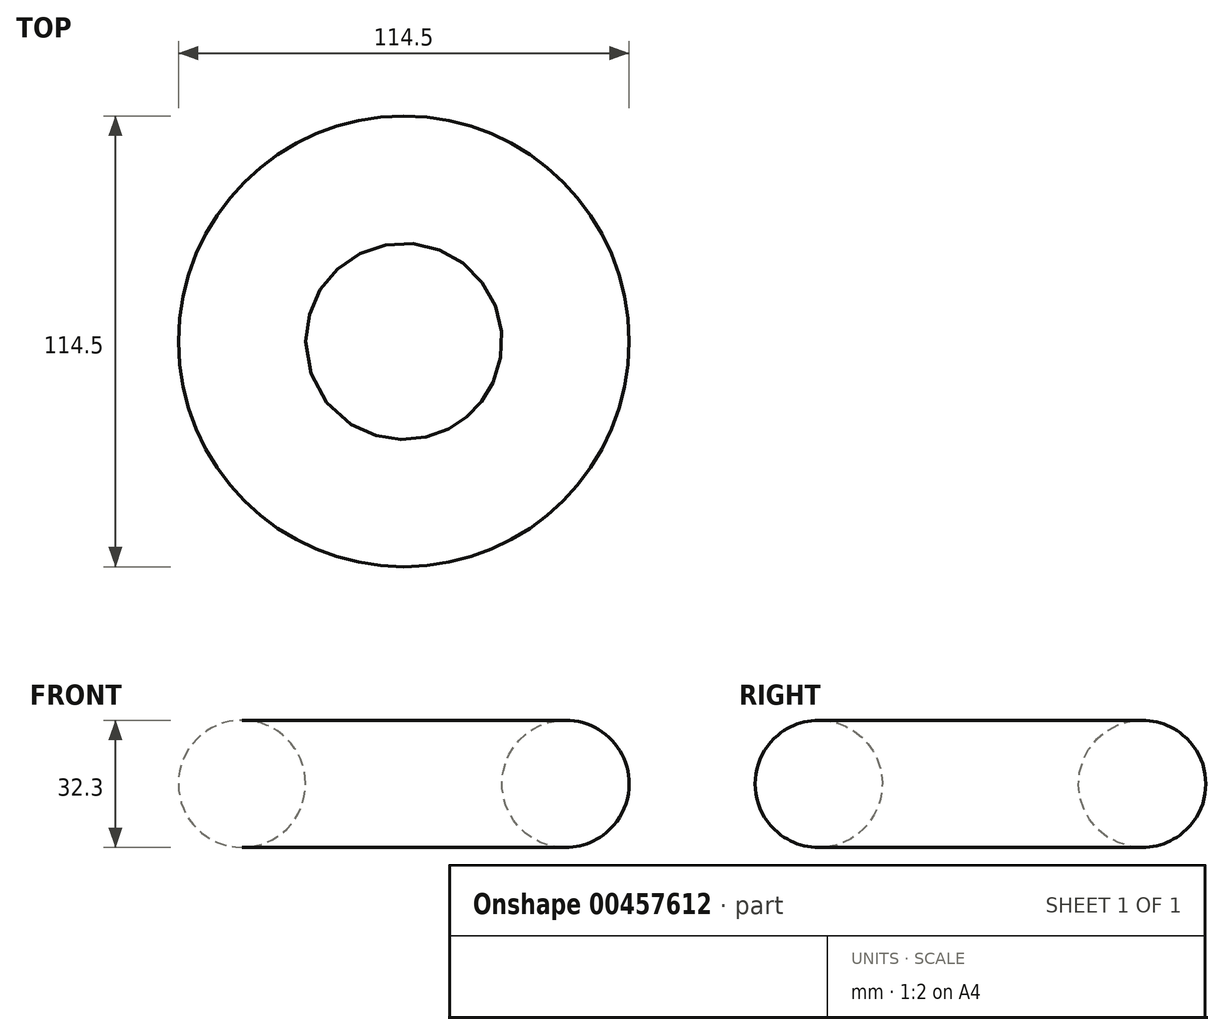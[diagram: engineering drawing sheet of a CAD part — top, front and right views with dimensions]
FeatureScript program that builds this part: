
annotation { "Feature Type Name" : "Feature", "Feature Type Description" : "" }
export const myFeature = defineFeature(function(context is Context, id is Id, definition is map)
    precondition{}
    {
        {
            var Q0;
            Q0=qCreatedBy(makeId("Front.planeOp"),FACE);
            var sketch = newSketch(context, id + "F0", { "sketchPlane" : qUnion([Q0])});
            skCircle(sketch, "E0", {"center": v(41.1, 0) * mm, "radius": 16.15 * mm});
            skLineSegment(sketch, "E1", {"start": v(0, 0) * mm, "end": v(0, 55.35) * mm, "construction": true});
            skSolve(sketch);
        }
        {
            var Q0;
            Q0=makeQuery(id+"F0.imprint","IMPRINT",FACE,{"disambiguationData":[TD([[makeQuery(id+"F0.imprint","IMPRINT",EDGE,{"derivedFrom":sQuery(id+"F0.wireOp",EDGE,"E0")}),1.0]])]});
            var Q1;
            Q1=sQuery(id+"F0.wireOp",EDGE,"E1");
            revolve(context, id + "F1", {"entities" : qUnion([Q0]), "axis" : qUnion([Q1]), "revolveType" : RevolveType.FULL});
        }
    });
